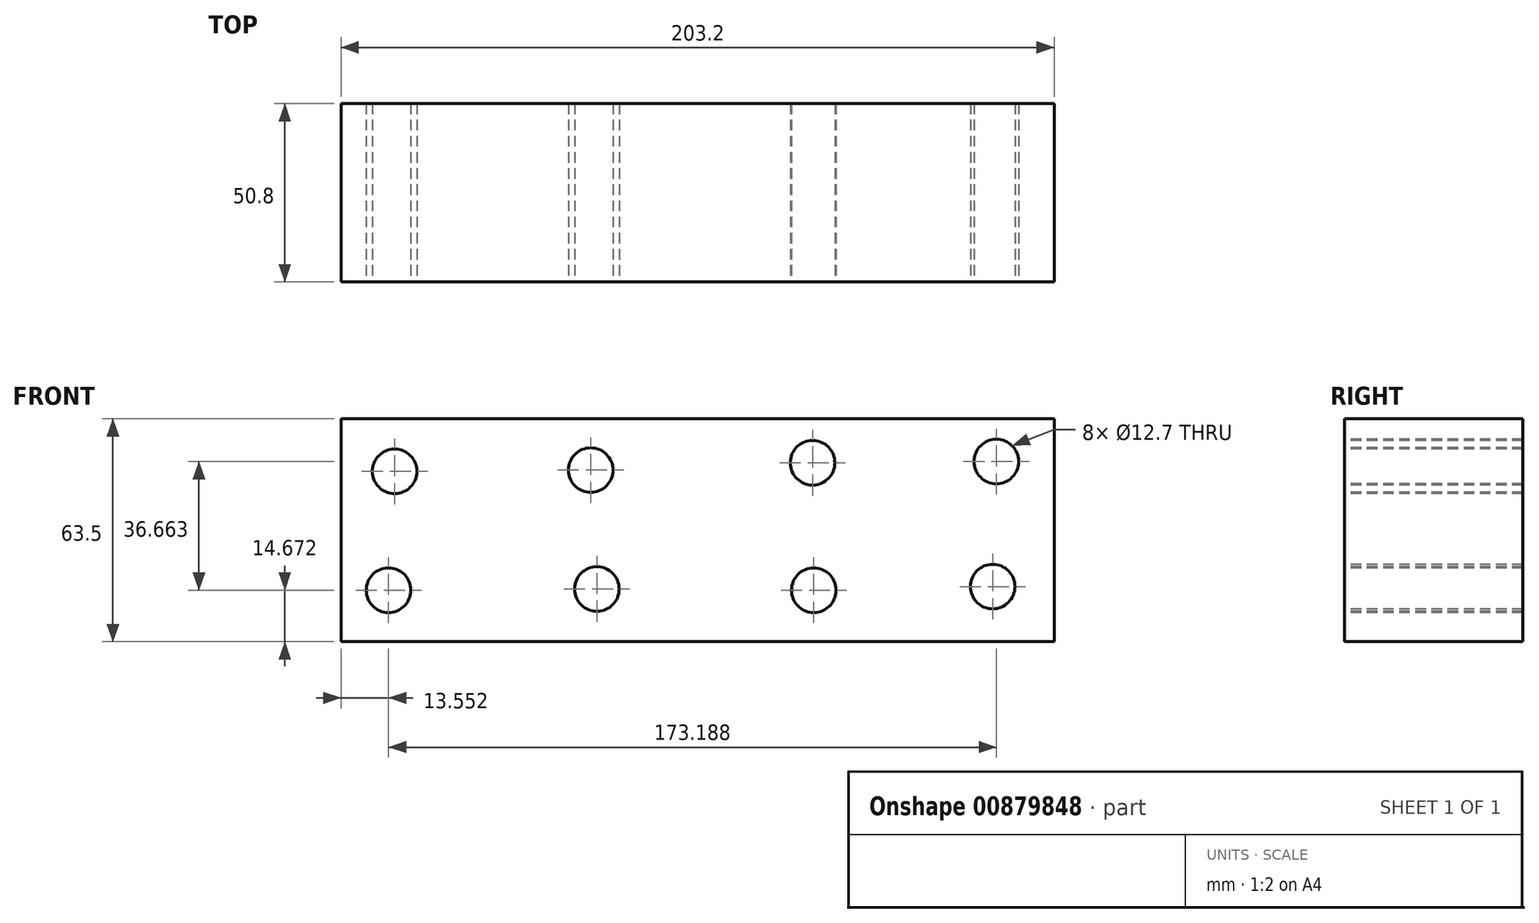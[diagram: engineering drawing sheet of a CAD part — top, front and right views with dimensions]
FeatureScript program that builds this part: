
annotation { "Feature Type Name" : "Feature", "Feature Type Description" : "" }
export const myFeature = defineFeature(function(context is Context, id is Id, definition is map)
    precondition{}
    {
        {
            var Q0;
            Q0=qCreatedBy(makeId("Front.planeOp"),FACE);
            var sketch = newSketch(context, id + "F0", { "sketchPlane" : qUnion([Q0])});
            skLineSegment(sketch, "E0.bottom", {"start": v(-129.62, 38.02) * mm, "end": v(73.58, 38.02) * mm});
            skLineSegment(sketch, "E0.top", {"start": v(-129.62, -25.48) * mm, "end": v(73.58, -25.48) * mm});
            skLineSegment(sketch, "E0.left", {"start": v(-129.62, 38.02) * mm, "end": v(-129.62, -25.48) * mm});
            skLineSegment(sketch, "E0.right", {"start": v(73.58, 38.02) * mm, "end": v(73.58, -25.48) * mm});
            skCircle(sketch, "E1", {"center": v(-114.32, 23.06) * mm, "radius": 6.35 * mm});
            skCircle(sketch, "E2", {"center": v(-116.07, -10.8) * mm, "radius": 6.35 * mm});
            skCircle(sketch, "E3", {"center": v(-58.45, 23.41) * mm, "radius": 6.35 * mm});
            skCircle(sketch, "E4", {"center": v(-56.7, -10.46) * mm, "radius": 6.35 * mm});
            skCircle(sketch, "E5", {"center": v(4.74, 25.5) * mm, "radius": 6.35 * mm});
            skCircle(sketch, "E6", {"center": v(5.1, -10.8) * mm, "radius": 6.35 * mm});
            skCircle(sketch, "E7", {"center": v(57.12, 25.85) * mm, "radius": 6.35 * mm});
            skCircle(sketch, "E8", {"center": v(56.07, -9.76) * mm, "radius": 6.35 * mm});
            skSolve(sketch);
        }
        {
            var Q0;
            Q0=makeQuery(id+"F0.imprint","IMPRINT",FACE,{"disambiguationData":[TD([[makeQuery(id+"F0.imprint","IMPRINT",EDGE,{"derivedFrom":sQuery(id+"F0.wireOp",EDGE,"E0.bottom")}),-1.0]])]});
            extrude(context, id + "F1", {"entities" : qUnion([Q0]), "oppositeDirection" : true, "depth" : 50.8 * mm, "offsetDistance" : 25.4 * mm});
        }
    });
